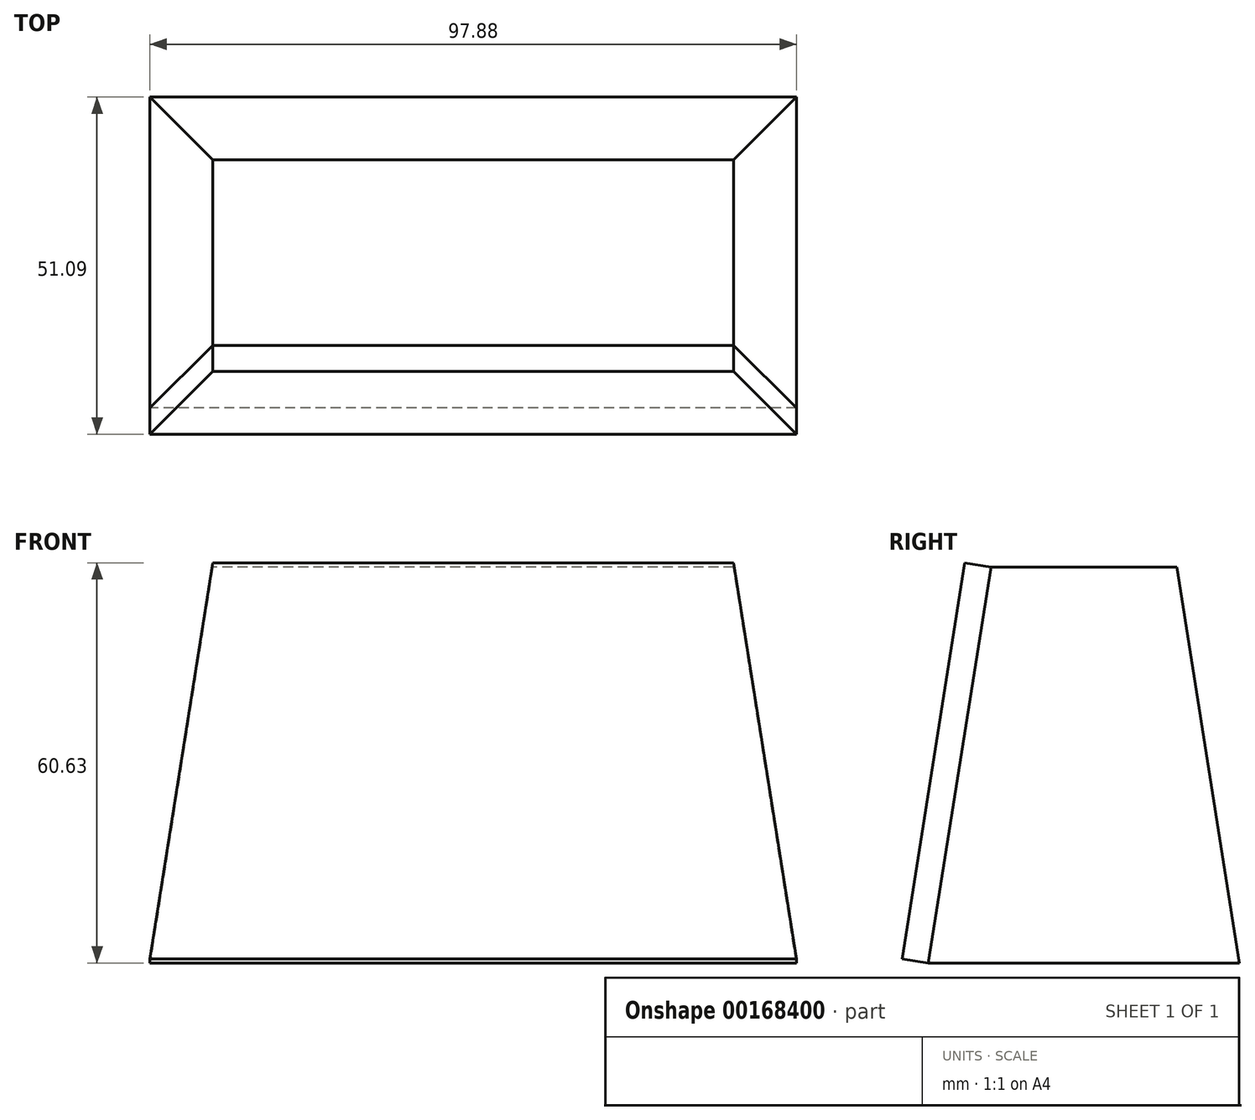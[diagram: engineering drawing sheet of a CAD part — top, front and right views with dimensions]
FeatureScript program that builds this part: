
annotation { "Feature Type Name" : "Feature", "Feature Type Description" : "" }
export const myFeature = defineFeature(function(context is Context, id is Id, definition is map)
    precondition{}
    {
        {
            var Q0;
            Q0=qCreatedBy(makeId("Top.planeOp"),FACE);
            var sketch = newSketch(context, id + "F0", { "sketchPlane" : qUnion([Q0])});
            skLineSegment(sketch, "E0.bottom", {"start": v(-58.29, 25.08) * mm, "end": v(39.59, 25.08) * mm});
            skLineSegment(sketch, "E0.top", {"start": v(-58.29, -22.06) * mm, "end": v(39.59, -22.06) * mm});
            skLineSegment(sketch, "E0.left", {"start": v(-58.29, 25.08) * mm, "end": v(-58.29, -22.06) * mm});
            skLineSegment(sketch, "E0.right", {"start": v(39.59, 25.08) * mm, "end": v(39.59, -22.06) * mm});
            skSolve(sketch);
        }
        {
            var Q0;
            Q0=makeQuery(id+"F0.imprint","IMPRINT",FACE,{"disambiguationData":[TD([[makeQuery(id+"F0.imprint","IMPRINT",EDGE,{"derivedFrom":sQuery(id+"F0.wireOp",EDGE,"E0.bottom")}),-1.0]])]});
            extrude(context, id + "F1", {"entities" : qUnion([Q0]), "depth" : 60 * mm, "hasDraft" : true, "draftAngle" : 9 * degree, "draftPullDirection" : true});
        }
        {
            var Q0;
            Q0=makeQuery(id+"F1.opExtrude","SWEPT_FACE",FACE,{"disambiguationData":[OSD([sQuery(id+"F0.wireOp",EDGE,"E0.top")])]});
            extrude(context, id + "F2", {"entities" : qUnion([Q0]), "depth" : 4 * mm});
        }
    });
